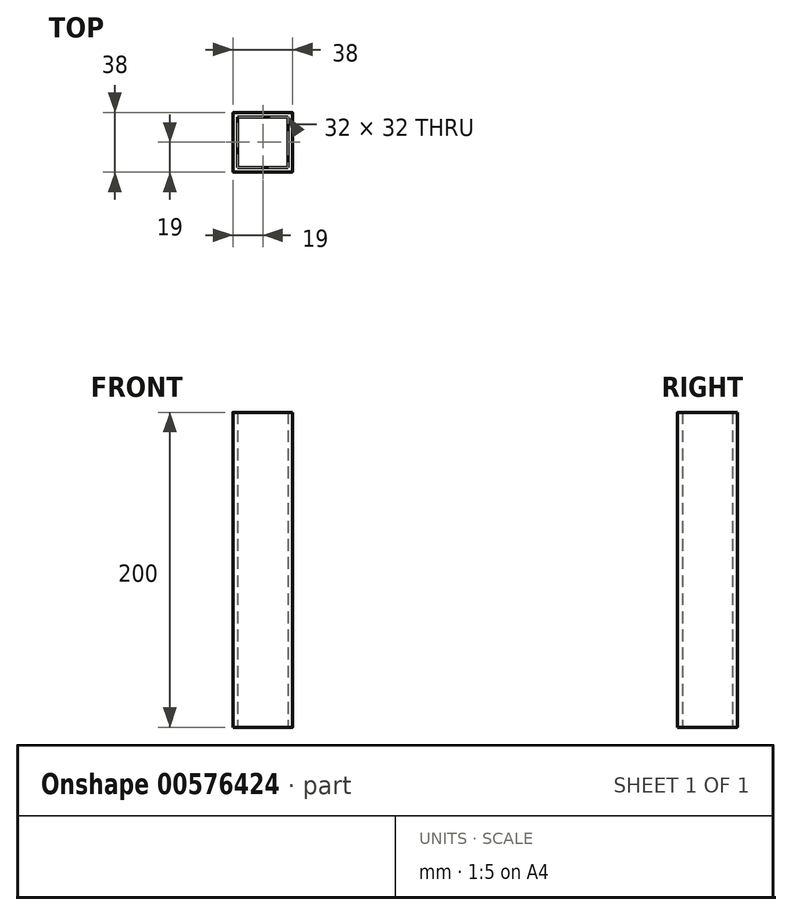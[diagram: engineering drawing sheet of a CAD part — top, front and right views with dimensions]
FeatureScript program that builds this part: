
annotation { "Feature Type Name" : "Feature", "Feature Type Description" : "" }
export const myFeature = defineFeature(function(context is Context, id is Id, definition is map)
    precondition{}
    {
        {
            var Q0;
            Q0=qCreatedBy(makeId("Top.planeOp"),FACE);
            var sketch = newSketch(context, id + "F0", { "sketchPlane" : qUnion([Q0])});
            skLineSegment(sketch, "E0.bottom", {"start": v(-19, -19) * mm, "end": v(19, -19) * mm});
            skLineSegment(sketch, "E0.top", {"start": v(-19, 19) * mm, "end": v(19, 19) * mm});
            skLineSegment(sketch, "E0.left", {"start": v(-19, -19) * mm, "end": v(-19, 19) * mm});
            skLineSegment(sketch, "E0.right", {"start": v(19, -19) * mm, "end": v(19, 19) * mm});
            skPoint(sketch, "E0.middle", {"position": v(0, 0) * mm});
            skLineSegment(sketch, "E1.0", {"start": v(-16, -16) * mm, "end": v(16, -16) * mm});
            skLineSegment(sketch, "E1.1", {"start": v(-16, -16) * mm, "end": v(-16, 16) * mm});
            skLineSegment(sketch, "E1.2", {"start": v(-16, 16) * mm, "end": v(16, 16) * mm});
            skLineSegment(sketch, "E1.3", {"start": v(16, -16) * mm, "end": v(16, 16) * mm});
            skSolve(sketch);
        }
        {
            var Q0;
            Q0=makeQuery(id+"F0.imprint","IMPRINT",FACE,{"disambiguationData":[TD([[makeQuery(id+"F0.imprint","IMPRINT",EDGE,{"derivedFrom":sQuery(id+"F0.wireOp",EDGE,"E0.bottom")}),1.0]])]});
            extrude(context, id + "F1", {"entities" : qUnion([Q0]), "depth" : 200 * mm, "offsetDistance" : 25 * mm});
        }
        {
            var Q0;
            Q0=makeQuery(id+"F1.opExtrude","SWEPT_EDGE",EDGE,{"disambiguationData":[OSD([sQuery(id+"F0.wireOp",EDGE,"E0.bottom"),sQuery(id+"F0.wireOp",EDGE,"E0.left")])]});
            var Q1;
            Q1=makeQuery(id+"F1.opExtrude","SWEPT_EDGE",EDGE,{"disambiguationData":[OSD([sQuery(id+"F0.wireOp",EDGE,"E0.bottom"),sQuery(id+"F0.wireOp",EDGE,"E0.right")])]});
            var Q2;
            Q2=makeQuery(id+"F1.opExtrude","SWEPT_EDGE",EDGE,{"disambiguationData":[OSD([sQuery(id+"F0.wireOp",EDGE,"E0.top"),sQuery(id+"F0.wireOp",EDGE,"E0.right")])]});
            var Q3;
            Q3=makeQuery(id+"F1.opExtrude","SWEPT_EDGE",EDGE,{"disambiguationData":[OSD([sQuery(id+"F0.wireOp",EDGE,"E0.top"),sQuery(id+"F0.wireOp",EDGE,"E0.left")])]});
            fillet(context, id + "F2", {"entities" : qUnion([Q0, Q1, Q2, Q3]), "radius" : 0.5 * mm, "tangentPropagation" : true, "allowEdgeOverflow" : false});
        }
    });
